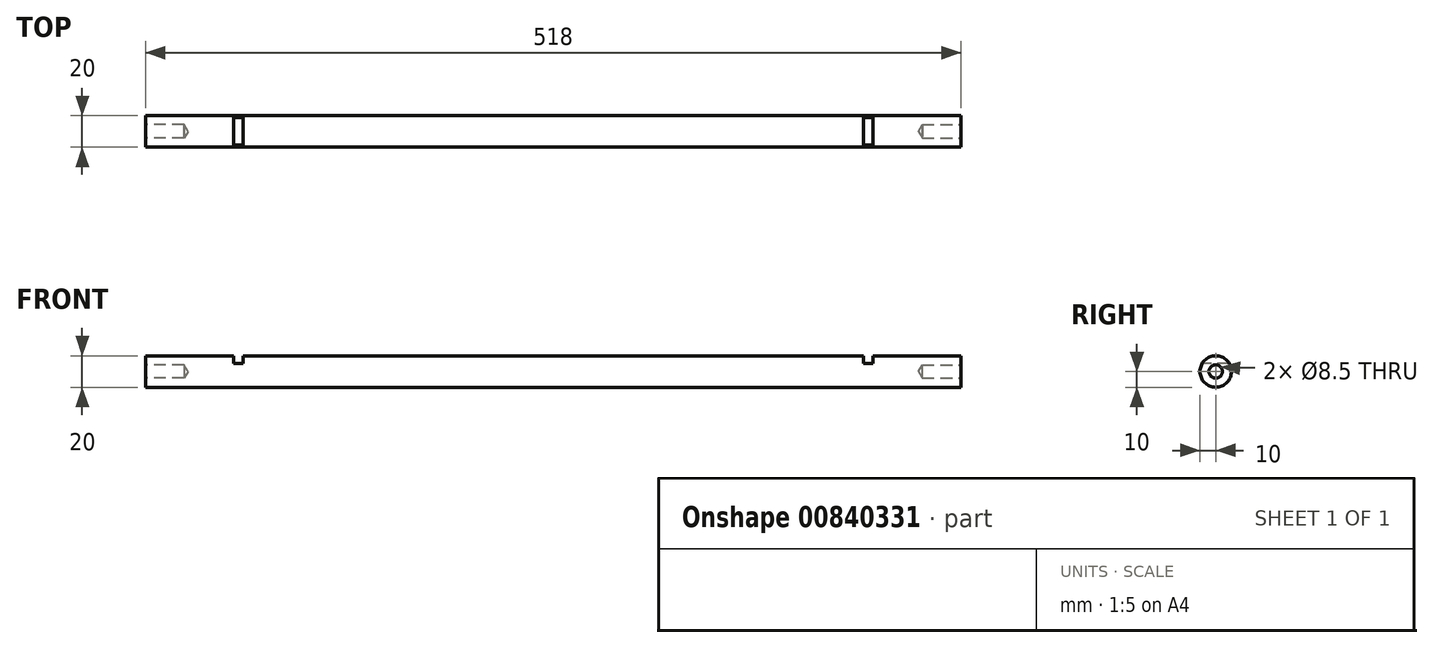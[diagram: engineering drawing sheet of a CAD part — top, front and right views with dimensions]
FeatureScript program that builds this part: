
annotation { "Feature Type Name" : "Feature", "Feature Type Description" : "" }
export const myFeature = defineFeature(function(context is Context, id is Id, definition is map)
    precondition{}
    {
        {
            var Q0;
            Q0=qCreatedBy(makeId("Right.planeOp"),FACE);
            var sketch = newSketch(context, id + "F0", { "sketchPlane" : qUnion([Q0])});
            skCircle(sketch, "E0", {"center": v(0, 0) * mm, "radius": 10 * mm});
            skSolve(sketch);
        }
        {
            var Q0;
            Q0 = qSketchRegion(id + "F0", true);
            extrude(context, id + "F1", {"entities" : qUnion([Q0]), "endBound" : BoundingType.SYMMETRIC, "depth" : 518 * mm, "offsetDistance" : 25 * mm});
        }
        {
            var Q0;
            Q0=qCreatedBy(makeId("Front.planeOp"),FACE);
            var sketch = newSketch(context, id + "F2", { "sketchPlane" : qUnion([Q0])});
            skLineSegment(sketch, "E1.bottom", {"start": v(-203, 10) * mm, "end": v(-197, 10) * mm});
            skLineSegment(sketch, "E1.top", {"start": v(-203, 5) * mm, "end": v(-197, 5) * mm});
            skLineSegment(sketch, "E1.left", {"start": v(-203, 10) * mm, "end": v(-203, 5) * mm});
            skLineSegment(sketch, "E1.right", {"start": v(-197, 10) * mm, "end": v(-197, 5) * mm});
            skLineSegment(sketch, "E2.bottom", {"start": v(197, 10) * mm, "end": v(203, 10) * mm});
            skLineSegment(sketch, "E2.top", {"start": v(197, 5) * mm, "end": v(203, 5) * mm});
            skLineSegment(sketch, "E2.left", {"start": v(197, 10) * mm, "end": v(197, 5) * mm});
            skLineSegment(sketch, "E2.right", {"start": v(203, 10) * mm, "end": v(203, 5) * mm});
            skSolve(sketch);
        }
        {
            var Q0;
            Q0 = qSketchRegion(id + "F2", true);
            extrude(context, id + "F3", {"entities" : qUnion([Q0]), "operationType" : NewBodyOperationType.REMOVE, "endBound" : BoundingType.THROUGH_ALL, "oppositeDirection" : true, "depth" : 25 * mm, "offsetDistance" : 25 * mm, "hasSecondDirection" : true, "secondDirectionBound" : SecondDirectionBoundingType.THROUGH_ALL, "secondDirectionOppositeDirection" : false, "secondDirectionDepth" : 25 * mm});
        }
        {
            var Q0;
            Q0=makeQuery(id+"F1.opExtrude","CAP_FACE",FACE,{"disambiguationData":[OSD([sQuery(id+"F0.wireOp",EDGE,"E0")])],"isStart":false});
            var sketch = newSketch(context, id + "F4", { "sketchPlane" : qUnion([Q0])});
            skPoint(sketch, "E3", {"position": v(0, 0) * mm});
            skSolve(sketch);
        }
        {
            var Q0;
            Q0=makeQuery(id+"F1.opExtrude","CAP_FACE",FACE,{"disambiguationData":[OSD([sQuery(id+"F0.wireOp",EDGE,"E0")])],"isStart":true});
            var sketch = newSketch(context, id + "F5", { "sketchPlane" : qUnion([Q0])});
            skPoint(sketch, "E4", {"position": v(0, 0) * mm});
            skSolve(sketch);
        }
        {
            var Q0;
            Q0=sQuery(id+"F5.wireOp",VERTEX,"E4");
            var Q1;
            Q1=sQuery(id+"F4.wireOp",VERTEX,"E3");
            var Q2;
            Q2=makeQuery(id+"F1.opExtrude","SWEPT_BODY",BODY,{"disambiguationData":[OSD([sQuery(id+"F0.wireOp",EDGE,"E0")])]});
            hole(context, id + "F6", {"style" : HoleStyle.SIMPLE, "endStyle" : HoleEndStyle.BLIND, "standardTappedOrClearance" : lookupTablePath({ "standard" : "ISO", "engagement" : "75%", "pitch" : "1.5 mm", "size" : "M10", "type" : "Tapped" }), "standardBlindInLast" : lookupTablePath({ "standard" : "ISO", "engagement" : "75%", "pitch" : "1.5 mm", "size" : "M10", "type" : "Tapped" }), "holeDiameter" : 8.5 * mm, "majorDiameter" : 10 * mm, "showTappedDepth" : true, "holeDepth" : 24.5 * mm, "isTappedThrough" : true, "tappedDepth" : 20 * mm, "tapClearance" : 3, "startFromSketch" : true, "locations" : qUnion([Q0, Q1]), "scope" : qUnion([Q2])});
        }
    });
